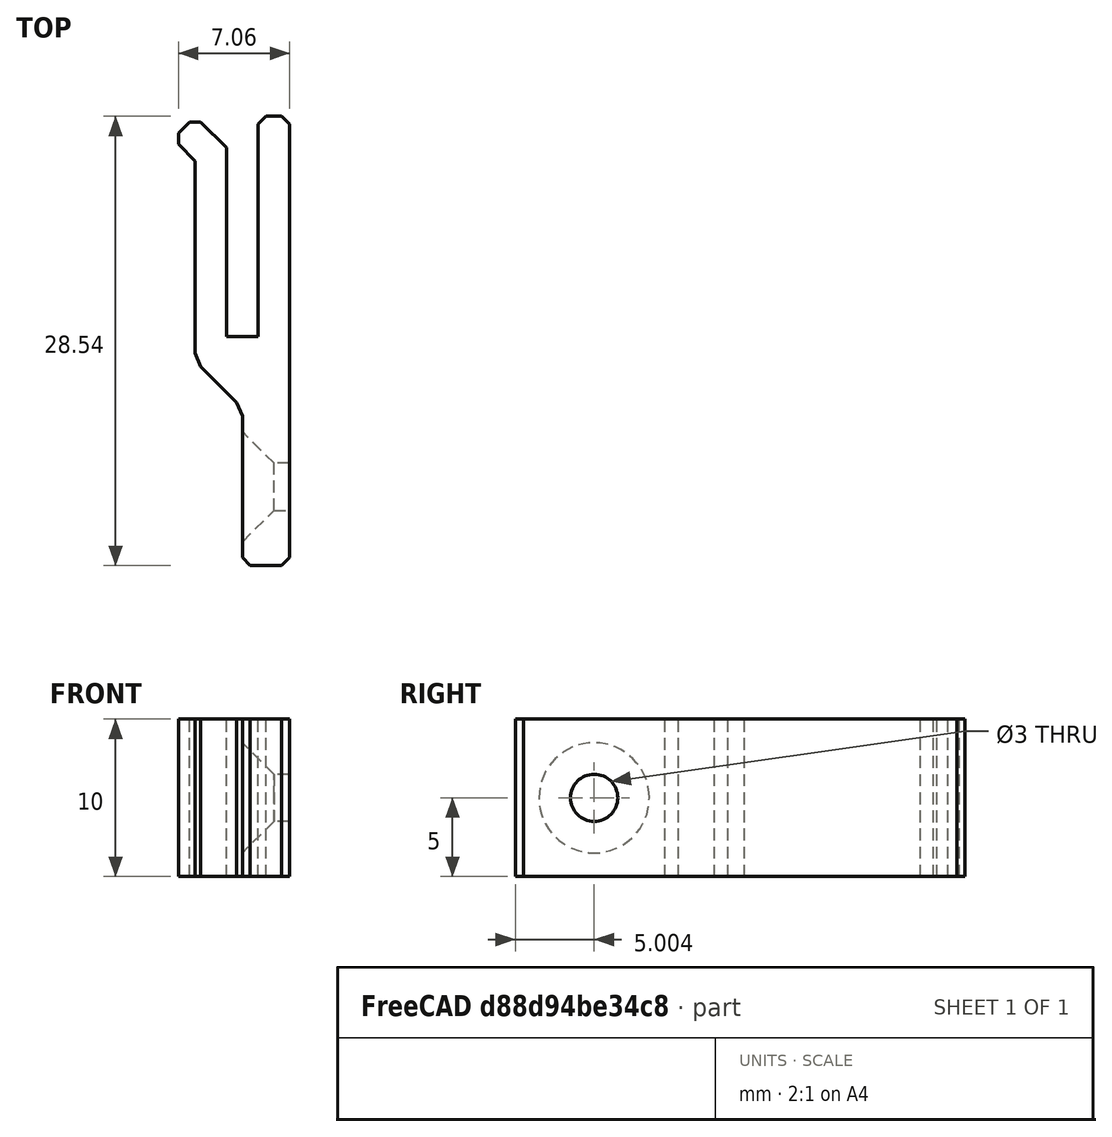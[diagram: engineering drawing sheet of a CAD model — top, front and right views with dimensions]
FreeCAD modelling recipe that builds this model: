
FCSTD DOCUMENT  (FreeCAD 0.18R16110 (Git))
Label: Fixation_bande_LED
License: All rights reserved
LicenseURL: http://en.wikipedia.org/wiki/All_rights_reserved
objects: Sketcher::SketchObject×2, PartDesign::Chamfer×2, PartDesign::Pad×1, PartDesign::Pocket×1, PartDesign::Body×1, Mesh::Feature×1
note: 9 computed .brp shape members not serialized (recipe doc carries the construction recipe); baked Part::Feature solids carry a one-line shape summary decoded from their .brp

FEATURE [Sketcher::SketchObject] Sketch
  MapMode = 5
  Support = -> [XY_Plane]
  sketch-geometry (12):
    g0: LineSegment StartX=0 StartY=14 StartZ=0 EndX=0 EndY=0 EndZ=0
    g1: LineSegment StartX=0 StartY=0 StartZ=0 EndX=-2 EndY=0 EndZ=0
    g2: LineSegment StartX=-2 StartY=0 StartZ=0 EndX=-2 EndY=12 EndZ=0
    g3: LineSegment StartX=-2 StartY=12 StartZ=0 EndX=-4 EndY=14 EndZ=0
    g4: LineSegment StartX=-4 StartY=14 StartZ=0 EndX=-5.41421 EndY=12.5858 EndZ=0
    g5: LineSegment StartX=-5.41421 StartY=12.5858 StartZ=0 EndX=-4 EndY=11.1716 EndZ=0
    g6: LineSegment StartX=-4 StartY=11.1716 StartZ=0 EndX=-4 EndY=-1.53553 EndZ=0
    g7: LineSegment StartX=-4 StartY=-1.53553 StartZ=0 EndX=-1 EndY=-4.53553 EndZ=0
    g8: LineSegment StartX=-1 StartY=-4.53553 StartZ=0 EndX=-1 EndY=-14.5355 EndZ=0
    g9: LineSegment StartX=-1 StartY=-14.5355 StartZ=0 EndX=2 EndY=-14.5355 EndZ=0
    g10: LineSegment StartX=2 StartY=-14.5355 StartZ=0 EndX=2 EndY=14 EndZ=0
    g11: LineSegment StartX=2 StartY=14 StartZ=0 EndX=0 EndY=14 EndZ=0
  constraints (35):
    c: PointOnObject(g0,g-2)
    c: Coincident(g0,g-1)
    c: Coincident(g0,g1)
    c: PointOnObject(g1,g-1)
    c: Coincident(g1,g2)
    c: Vertical(g2)
    c: Coincident(g2,g3)
    c: Coincident(g3,g4)
    c: Coincident(g4,g5)
    c: Coincident(g5,g6)
    c: Vertical(g6)
    c: Coincident(g6,g7)
    c: Coincident(g7,g8)
    c: Coincident(g8,g9)
    c: Horizontal(g9)
    c: Coincident(g9,g10)
    c: Vertical(g10)
    c: Coincident(g10,g11)
    c: Coincident(g11,g0)
    c: DistanceX(g1,g1) = 2
    c: Horizontal(g11)
    c: Distance(g5,g2) = 2
    c: Distance(g4) = 2
    c: Angle(g5,g6) = 2.35619
    c: Angle(g3) = 2.35619
    c: Perpendicular(g5,g4)
    c: DistanceY(g0,g0) = 14
    c: Distance(g3,g1) = 14
    c: Angle(g7,g6) = 2.35619
    c: DistanceY(g8,g8) = 10
    c: Distance(g1,g7) = 2.5
    c: DistanceY(g2,g2) = 12
    c: Vertical(g8)
    c: DistanceX(g9,g9) = 3
    c: DistanceX(g11,g11) = 2
FEATURE [PartDesign::Pad] Pad
  Length = 10
  Length2 = 100
  Profile = -> Sketch
  Type = 0
FEATURE [Sketcher::SketchObject] Sketch001
  ExternalGeometry = -> [Pad]
  MapMode = 5
  Placement = pos=(-1,0,0) rot=(0.57735,-0.57735,-0.57735;2.0944rad)
  Support = -> [Pad]
  sketch-geometry (1):
    g0: Circle CenterX=9.53553 CenterY=5 CenterZ=0 NormalX=0 NormalY=0 NormalZ=1 AngleXU=0 Radius=1.5
  constraints (3):
    c: DistanceY(g-1,g0) = 5
    c: Distance(g0,g-4) = 5
    c: Radius(g0) = 1.5
FEATURE [PartDesign::Pocket] Pocket
  BaseFeature = -> Pad
  Length = 5
  Length2 = 100
  Profile = -> Sketch001
  Type = 0
FEATURE [PartDesign::Chamfer] Chamfer
  Base = -> Pocket [Edge38]
  BaseFeature = -> Pocket
  Size = 2
FEATURE [PartDesign::Chamfer] Chamfer001
  Base = -> Chamfer [Edge40,Edge39,Edge35,Edge8,Edge2,Edge5,Edge31,Edge41]
  BaseFeature = -> Chamfer
  Size = 0.5
FEATURE [PartDesign::Body] Body
  Group = -> [Sketch,Pad,Sketch001,Pocket,Chamfer,Chamfer001]
  Origin = -> Origin
  Tip = -> Chamfer001
FEATURE [Mesh::Feature] Mesh  label="Body (Meshed)"
